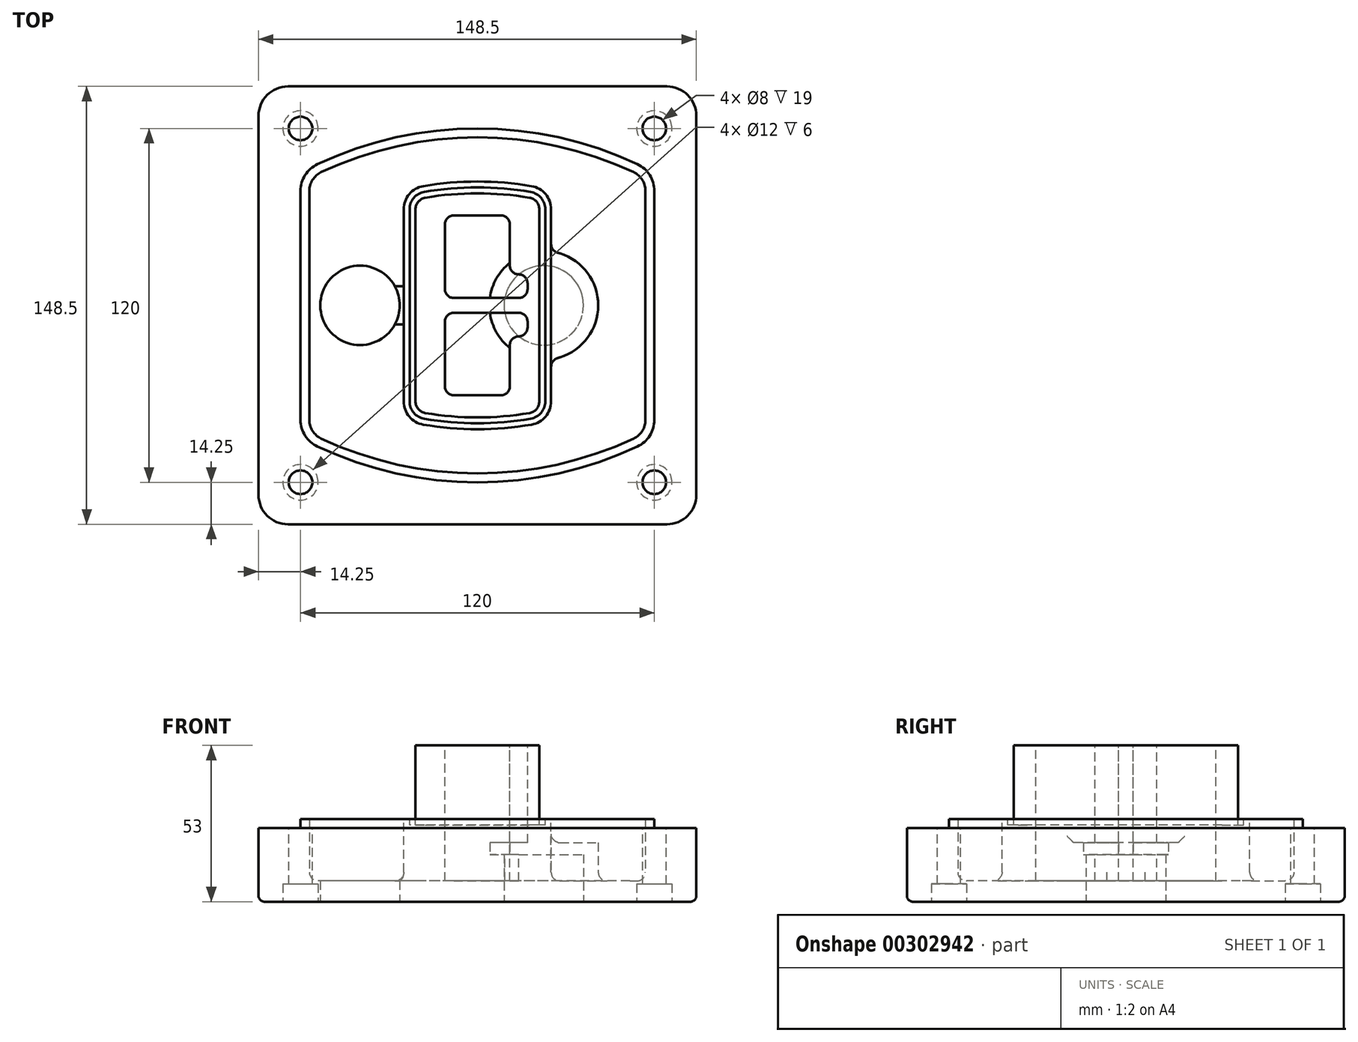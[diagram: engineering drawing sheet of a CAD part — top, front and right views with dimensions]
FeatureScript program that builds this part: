
annotation { "Feature Type Name" : "Feature", "Feature Type Description" : "" }
export const myFeature = defineFeature(function(context is Context, id is Id, definition is map)
    precondition{}
    {
        {
            var Q0;
            Q0=qCreatedBy(makeId("Top.planeOp"),FACE);
            var sketch = newSketch(context, id + "F0", { "sketchPlane" : qUnion([Q0])});
            skPoint(sketch, "E0.rect.middle", {"position": v(0, 0) * mm});
            skLineSegment(sketch, "E1.bottom", {"start": v(-64.25, -74.25) * mm, "end": v(64.25, -74.25) * mm});
            skLineSegment(sketch, "E1.top", {"start": v(-64.25, 74.25) * mm, "end": v(64.25, 74.25) * mm});
            skLineSegment(sketch, "E1.left", {"start": v(-74.25, -64.25) * mm, "end": v(-74.25, 64.25) * mm});
            skLineSegment(sketch, "E1.right", {"start": v(74.25, -64.25) * mm, "end": v(74.25, 64.25) * mm});
            skLineSegment(sketch, "E2", {"start": v(-74.25, 74.25) * mm, "end": v(74.25, -74.25) * mm, "construction": true});
            skLineSegment(sketch, "E3", {"start": v(74.25, 74.25) * mm, "end": v(-74.25, -74.25) * mm, "construction": true});
            skCircle(sketch, "E4", {"center": v(-60, 60) * mm, "radius": 4 * mm});
            skCircle(sketch, "E5", {"center": v(60, 60) * mm, "radius": 4 * mm});
            skCircle(sketch, "E6", {"center": v(60, -60) * mm, "radius": 4 * mm});
            skCircle(sketch, "E7", {"center": v(-60, -60) * mm, "radius": 4 * mm});
            skLineSegment(sketch, "E8", {"start": v(-60, 60) * mm, "end": v(60, 60) * mm, "construction": true});
            skLineSegment(sketch, "E9", {"start": v(60, 60) * mm, "end": v(60, -60) * mm, "construction": true});
            skLineSegment(sketch, "E10", {"start": v(60, -60) * mm, "end": v(-60, -60) * mm, "construction": true});
            skLineSegment(sketch, "E11", {"start": v(-60, -60) * mm, "end": v(-60, 60) * mm, "construction": true});
            skLineSegment(sketch, "E12", {"start": v(-60, 38.83) * mm, "end": v(-60, -38.83) * mm});
            skLineSegment(sketch, "E13", {"start": v(60, 38.83) * mm, "end": v(60, -38.83) * mm});
            skArc(sketch, "E14", {"start": v(54.26, 47.88) * mm, "mid": v(0, 60) * mm, "end": v(-54.26, 47.88) * mm});
            skArc(sketch, "E15", {"start": v(-54.26, -47.88) * mm, "mid": v(0, -60) * mm, "end": v(54.26, -47.88) * mm});
            skLineSegment(sketch, "E16", {"start": v(-60, 0) * mm, "end": v(60, 0) * mm, "construction": true});
            skPoint(sketch, "E17.visualSharp", {"position": v(-60, -45) * mm});
            skArc(sketch, "E17.filletArc", {"start": v(-60, -38.83) * mm, "mid": v(-58.44, -44.2) * mm, "end": v(-54.26, -47.88) * mm});
            skPoint(sketch, "E18.visualSharp", {"position": v(-60, 45) * mm});
            skArc(sketch, "E18.filletArc", {"start": v(-54.26, 47.88) * mm, "mid": v(-58.44, 44.2) * mm, "end": v(-60, 38.83) * mm});
            skPoint(sketch, "E19.visualSharp", {"position": v(60, 45) * mm});
            skArc(sketch, "E19.filletArc", {"start": v(60, 38.83) * mm, "mid": v(58.44, 44.2) * mm, "end": v(54.26, 47.88) * mm});
            skPoint(sketch, "E20.visualSharp", {"position": v(60, -45) * mm});
            skArc(sketch, "E20.filletArc", {"start": v(54.26, -47.88) * mm, "mid": v(58.44, -44.2) * mm, "end": v(60, -38.83) * mm});
            skPoint(sketch, "E21.visualSharp", {"position": v(-74.25, 74.25) * mm});
            skArc(sketch, "E21.filletArc", {"start": v(-64.25, 74.25) * mm, "mid": v(-71.32, 71.32) * mm, "end": v(-74.25, 64.25) * mm});
            skPoint(sketch, "E22.visualSharp", {"position": v(74.25, 74.25) * mm});
            skArc(sketch, "E22.filletArc", {"start": v(74.25, 64.25) * mm, "mid": v(71.32, 71.32) * mm, "end": v(64.25, 74.25) * mm});
            skPoint(sketch, "E23.visualSharp", {"position": v(74.25, -74.25) * mm});
            skArc(sketch, "E23.filletArc", {"start": v(64.25, -74.25) * mm, "mid": v(71.32, -71.32) * mm, "end": v(74.25, -64.25) * mm});
            skPoint(sketch, "E24.visualSharp", {"position": v(-74.25, -74.25) * mm});
            skArc(sketch, "E24.filletArc", {"start": v(-74.25, -64.25) * mm, "mid": v(-71.32, -71.32) * mm, "end": v(-64.25, -74.25) * mm});
            skArc(sketch, "E25.0", {"start": v(57, 38.83) * mm, "mid": v(55.9, 42.58) * mm, "end": v(52.98, 45.17) * mm});
            skLineSegment(sketch, "E25.1", {"start": v(57, 38.83) * mm, "end": v(57, -38.83) * mm});
            skArc(sketch, "E25.2", {"start": v(52.98, -45.17) * mm, "mid": v(55.9, -42.58) * mm, "end": v(57, -38.83) * mm});
            skArc(sketch, "E25.3", {"start": v(-52.98, -45.17) * mm, "mid": v(0, -57) * mm, "end": v(52.98, -45.17) * mm});
            skArc(sketch, "E25.4", {"start": v(-57, -38.83) * mm, "mid": v(-55.9, -42.58) * mm, "end": v(-52.98, -45.17) * mm});
            skArc(sketch, "E25.5", {"start": v(52.98, 45.17) * mm, "mid": v(0, 57) * mm, "end": v(-52.98, 45.17) * mm});
            skLineSegment(sketch, "E25.6", {"start": v(-57, 38.83) * mm, "end": v(-57, -38.83) * mm});
            skArc(sketch, "E25.7", {"start": v(-52.98, 45.17) * mm, "mid": v(-55.9, 42.58) * mm, "end": v(-57, 38.83) * mm});
            skArc(sketch, "E26.0", {"start": v(-55.96, 51.5) * mm, "mid": v(-61.82, 46.33) * mm, "end": v(-64, 38.83) * mm});
            skArc(sketch, "E26.1", {"start": v(55.96, 51.5) * mm, "mid": v(0, 64) * mm, "end": v(-55.96, 51.5) * mm});
            skArc(sketch, "E26.2", {"start": v(64, 38.83) * mm, "mid": v(61.82, 46.33) * mm, "end": v(55.96, 51.5) * mm});
            skLineSegment(sketch, "E26.3", {"start": v(64, 38.83) * mm, "end": v(64, -38.83) * mm});
            skArc(sketch, "E26.4", {"start": v(55.96, -51.5) * mm, "mid": v(61.82, -46.33) * mm, "end": v(64, -38.83) * mm});
            skLineSegment(sketch, "E26.5", {"start": v(-64, 38.83) * mm, "end": v(-64, -38.83) * mm});
            skArc(sketch, "E26.6", {"start": v(-55.96, -51.5) * mm, "mid": v(0, -64) * mm, "end": v(55.96, -51.5) * mm});
            skArc(sketch, "E26.7", {"start": v(-64, -38.83) * mm, "mid": v(-61.82, -46.33) * mm, "end": v(-55.96, -51.5) * mm});
            skSolve(sketch);
        }
        {
            var Q0;
            Q0=makeQuery(id+"F0.imprint","IMPRINT",FACE,{"disambiguationData":[TD([[makeQuery(id+"F0.imprint","IMPRINT",EDGE,{"derivedFrom":sQuery(id+"F0.wireOp",EDGE,"E1.bottom")}),1.0]])]});
            var Q1;
            Q1=makeQuery(id+"F0.imprint","IMPRINT",FACE,{"disambiguationData":[TD([[makeQuery(id+"F0.imprint","IMPRINT",EDGE,{"derivedFrom":sQuery(id+"F0.wireOp",EDGE,"E12")}),1.0]])]});
            var Q2;
            Q2=makeQuery(id+"F0.imprint","IMPRINT",FACE,{"disambiguationData":[TD([[makeQuery(id+"F0.imprint","IMPRINT",EDGE,{"derivedFrom":sQuery(id+"F0.wireOp",EDGE,"E25.0")}),1.0]])]});
            var Q3;
            Q3=makeQuery(id+"F0.imprint","IMPRINT",FACE,{"disambiguationData":[TD([[makeQuery(id+"F0.imprint","IMPRINT",EDGE,{"derivedFrom":sQuery(id+"F0.wireOp",EDGE,"E12")}),-1.0]])]});
            extrude(context, id + "F1", {"entities" : qUnion([Q0, Q1, Q2, Q3]), "oppositeDirection" : true, "depth" : 25 * mm});
        }
        {
            var Q0;
            Q0=makeQuery(id+"F0.imprint","IMPRINT",FACE,{"disambiguationData":[TD([[makeQuery(id+"F0.imprint","IMPRINT",EDGE,{"derivedFrom":sQuery(id+"F0.wireOp",EDGE,"E12")}),1.0]])]});
            extrude(context, id + "F2", {"entities" : qUnion([Q0]), "operationType" : NewBodyOperationType.ADD, "depth" : 3 * mm});
        }
        {
            var Q0;
            Q0=makeQuery(id+"F0.imprint","IMPRINT",FACE,{"disambiguationData":[TD([[makeQuery(id+"F0.imprint","IMPRINT",EDGE,{"derivedFrom":sQuery(id+"F0.wireOp",EDGE,"E25.0")}),1.0]])]});
            extrude(context, id + "F3", {"entities" : qUnion([Q0]), "operationType" : NewBodyOperationType.REMOVE, "oppositeDirection" : true, "depth" : 18 * mm});
        }
        {
            var Q0;
            Q0=makeQuery(id+"F2.opExtrude","CAP_FACE",FACE,{"disambiguationData":[OSD([sQuery(id+"F0.wireOp",EDGE,"E12"),sQuery(id+"F0.wireOp",EDGE,"E13"),sQuery(id+"F0.wireOp",EDGE,"E14"),sQuery(id+"F0.wireOp",EDGE,"E15"),sQuery(id+"F0.wireOp",EDGE,"E17.filletArc"),sQuery(id+"F0.wireOp",EDGE,"E18.filletArc"),sQuery(id+"F0.wireOp",EDGE,"E19.filletArc"),sQuery(id+"F0.wireOp",EDGE,"E20.filletArc"),sQuery(id+"F0.wireOp",EDGE,"E25.0"),sQuery(id+"F0.wireOp",EDGE,"E25.1"),sQuery(id+"F0.wireOp",EDGE,"E25.2"),sQuery(id+"F0.wireOp",EDGE,"E25.3"),sQuery(id+"F0.wireOp",EDGE,"E25.4"),sQuery(id+"F0.wireOp",EDGE,"E25.5"),sQuery(id+"F0.wireOp",EDGE,"E25.6"),sQuery(id+"F0.wireOp",EDGE,"E25.7")])],"isStart":false});
            var sketch = newSketch(context, id + "F4", { "sketchPlane" : qUnion([Q0])});
            skArc(sketch, "E27.0", {"start": v(-18.34, -40.45) * mm, "mid": v(0, -42) * mm, "end": v(18.34, -40.45) * mm});
            skArc(sketch, "E28.0", {"start": v(18.34, 40.45) * mm, "mid": v(0, 42) * mm, "end": v(-18.34, 40.45) * mm});
            skLineSegment(sketch, "E29", {"start": v(-25, 32.57) * mm, "end": v(-25, -32.57) * mm});
            skLineSegment(sketch, "E30", {"start": v(25, 32.57) * mm, "end": v(25, -32.57) * mm});
            skLineSegment(sketch, "E31", {"start": v(-25, 39.1) * mm, "end": v(25, 39.1) * mm, "construction": true});
            skLineSegment(sketch, "E32", {"start": v(-25, -39.1) * mm, "end": v(25, -39.1) * mm, "construction": true});
            skPoint(sketch, "E33.visualSharp", {"position": v(-25, 39.1) * mm});
            skArc(sketch, "E33.filletArc", {"start": v(-18.34, 40.45) * mm, "mid": v(-23.11, 37.73) * mm, "end": v(-25, 32.57) * mm});
            skPoint(sketch, "E34.visualSharp", {"position": v(25, 39.1) * mm});
            skArc(sketch, "E34.filletArc", {"start": v(25, 32.57) * mm, "mid": v(23.11, 37.73) * mm, "end": v(18.34, 40.45) * mm});
            skPoint(sketch, "E35.visualSharp", {"position": v(25, -39.1) * mm});
            skArc(sketch, "E35.filletArc", {"start": v(18.34, -40.45) * mm, "mid": v(23.11, -37.73) * mm, "end": v(25, -32.57) * mm});
            skPoint(sketch, "E36.visualSharp", {"position": v(-25, -39.1) * mm});
            skArc(sketch, "E36.filletArc", {"start": v(-25, -32.57) * mm, "mid": v(-23.11, -37.73) * mm, "end": v(-18.34, -40.45) * mm});
            skArc(sketch, "E37.0", {"start": v(52.98, 45.17) * mm, "mid": v(0, 57) * mm, "end": v(-52.98, 45.17) * mm});
            skArc(sketch, "E37.1", {"start": v(-52.98, 45.17) * mm, "mid": v(-55.9, 42.58) * mm, "end": v(-57, 38.83) * mm});
            skLineSegment(sketch, "E37.2", {"start": v(-57, 38.83) * mm, "end": v(-57, -38.83) * mm});
            skArc(sketch, "E37.3", {"start": v(-57, -38.83) * mm, "mid": v(-55.9, -42.58) * mm, "end": v(-52.98, -45.17) * mm});
            skArc(sketch, "E37.4", {"start": v(-52.98, -45.17) * mm, "mid": v(0, -57) * mm, "end": v(52.98, -45.17) * mm});
            skArc(sketch, "E37.5", {"start": v(52.98, -45.17) * mm, "mid": v(55.9, -42.58) * mm, "end": v(57, -38.83) * mm});
            skLineSegment(sketch, "E37.6", {"start": v(57, 38.83) * mm, "end": v(57, -38.83) * mm});
            skArc(sketch, "E37.7", {"start": v(57, 38.83) * mm, "mid": v(55.9, 42.58) * mm, "end": v(52.98, 45.17) * mm});
            skLineSegment(sketch, "E38.0", {"start": v(23, 32.57) * mm, "end": v(23, -32.57) * mm});
            skArc(sketch, "E38.1", {"start": v(18, -38.48) * mm, "mid": v(21.58, -36.44) * mm, "end": v(23, -32.57) * mm});
            skArc(sketch, "E38.2", {"start": v(-18, -38.48) * mm, "mid": v(0, -40) * mm, "end": v(18, -38.48) * mm});
            skArc(sketch, "E38.3", {"start": v(-23, -32.57) * mm, "mid": v(-21.58, -36.44) * mm, "end": v(-18, -38.48) * mm});
            skLineSegment(sketch, "E38.4", {"start": v(-23, 32.57) * mm, "end": v(-23, -32.57) * mm});
            skArc(sketch, "E38.5", {"start": v(23, 32.57) * mm, "mid": v(21.58, 36.44) * mm, "end": v(18, 38.48) * mm});
            skArc(sketch, "E38.6", {"start": v(-18, 38.48) * mm, "mid": v(-21.58, 36.44) * mm, "end": v(-23, 32.57) * mm});
            skArc(sketch, "E38.7", {"start": v(18, 38.48) * mm, "mid": v(0, 40) * mm, "end": v(-18, 38.48) * mm});
            skArc(sketch, "E39.0", {"start": v(21, 32.57) * mm, "mid": v(20.06, 35.15) * mm, "end": v(17.67, 36.5) * mm});
            skLineSegment(sketch, "E39.1", {"start": v(21, 32.57) * mm, "end": v(21, -32.57) * mm});
            skArc(sketch, "E39.2", {"start": v(17.67, -36.5) * mm, "mid": v(20.06, -35.15) * mm, "end": v(21, -32.57) * mm});
            skArc(sketch, "E39.3", {"start": v(-17.67, -36.5) * mm, "mid": v(0, -38) * mm, "end": v(17.67, -36.5) * mm});
            skArc(sketch, "E39.4", {"start": v(-21, -32.57) * mm, "mid": v(-20.06, -35.15) * mm, "end": v(-17.67, -36.5) * mm});
            skArc(sketch, "E39.5", {"start": v(17.67, 36.5) * mm, "mid": v(0, 38) * mm, "end": v(-17.67, 36.5) * mm});
            skLineSegment(sketch, "E39.6", {"start": v(-21, 32.57) * mm, "end": v(-21, -32.57) * mm});
            skArc(sketch, "E39.7", {"start": v(-17.67, 36.5) * mm, "mid": v(-20.06, 35.15) * mm, "end": v(-21, 32.57) * mm});
            skLineSegment(sketch, "E40", {"start": v(-25, 0) * mm, "end": v(25, 0) * mm, "construction": true});
            skLineSegment(sketch, "E41", {"start": v(-11, 5.5) * mm, "end": v(-11, 27.5) * mm});
            skLineSegment(sketch, "E42", {"start": v(-8, 30.5) * mm, "end": v(8, 30.5) * mm});
            skLineSegment(sketch, "E43", {"start": v(11, 27.5) * mm, "end": v(11, 13.5) * mm});
            skLineSegment(sketch, "E44", {"start": v(14, 10.5) * mm, "end": v(14, 10.5) * mm});
            skLineSegment(sketch, "E45", {"start": v(17, 7.5) * mm, "end": v(17, 5.5) * mm});
            skLineSegment(sketch, "E46", {"start": v(14, 2.5) * mm, "end": v(-8, 2.5) * mm});
            skPoint(sketch, "E47.visualSharp", {"position": v(-11, 30.5) * mm});
            skArc(sketch, "E47.filletArc", {"start": v(-8, 30.5) * mm, "mid": v(-10.12, 29.62) * mm, "end": v(-11, 27.5) * mm});
            skPoint(sketch, "E48.visualSharp", {"position": v(11, 30.5) * mm});
            skArc(sketch, "E48.filletArc", {"start": v(11, 27.5) * mm, "mid": v(10.12, 29.62) * mm, "end": v(8, 30.5) * mm});
            skPoint(sketch, "E49.visualSharp", {"position": v(11, 10.5) * mm});
            skArc(sketch, "E49.filletArc", {"start": v(11, 13.5) * mm, "mid": v(11.88, 11.38) * mm, "end": v(14, 10.5) * mm});
            skPoint(sketch, "E50.visualSharp", {"position": v(17, 10.5) * mm});
            skArc(sketch, "E50.filletArc", {"start": v(17, 7.5) * mm, "mid": v(16.12, 9.62) * mm, "end": v(14, 10.5) * mm});
            skPoint(sketch, "E51.visualSharp", {"position": v(17, 2.5) * mm});
            skArc(sketch, "E51.filletArc", {"start": v(14, 2.5) * mm, "mid": v(16.12, 3.38) * mm, "end": v(17, 5.5) * mm});
            skPoint(sketch, "E52.visualSharp", {"position": v(-11, 2.5) * mm});
            skArc(sketch, "E52.filletArc", {"start": v(-11, 5.5) * mm, "mid": v(-10.12, 3.38) * mm, "end": v(-8, 2.5) * mm});
            skLineSegment(sketch, "E53.0.MirrorCS", {"start": v(14, -2.5) * mm, "end": v(-8, -2.5) * mm});
            skArc(sketch, "E54.0.MirrorCS", {"start": v(-11, -5.5) * mm, "mid": v(-10.12, -3.38) * mm, "end": v(-8, -2.5) * mm});
            skLineSegment(sketch, "E55.0.MirrorCS", {"start": v(-11, -5.5) * mm, "end": v(-11, -27.5) * mm});
            skArc(sketch, "E56.0.MirrorCS", {"start": v(-8, -30.5) * mm, "mid": v(-10.12, -29.62) * mm, "end": v(-11, -27.5) * mm});
            skLineSegment(sketch, "E57.0.MirrorCS", {"start": v(-8, -30.5) * mm, "end": v(8, -30.5) * mm});
            skArc(sketch, "E58.0.MirrorCS", {"start": v(11, -27.5) * mm, "mid": v(10.12, -29.62) * mm, "end": v(8, -30.5) * mm});
            skLineSegment(sketch, "E59.0.MirrorCS", {"start": v(11, -27.5) * mm, "end": v(11, -13.5) * mm});
            skArc(sketch, "E60.0.MirrorCS", {"start": v(11, -13.5) * mm, "mid": v(11.88, -11.38) * mm, "end": v(14, -10.5) * mm});
            skArc(sketch, "E61.0.MirrorCS", {"start": v(17, -7.5) * mm, "mid": v(16.12, -9.62) * mm, "end": v(14, -10.5) * mm});
            skLineSegment(sketch, "E62.0.MirrorCS", {"start": v(17, -7.5) * mm, "end": v(17, -5.5) * mm});
            skArc(sketch, "E63.0.MirrorCS", {"start": v(14, -2.5) * mm, "mid": v(16.12, -3.38) * mm, "end": v(17, -5.5) * mm});
            skSolve(sketch);
        }
        {
            var Q0;
            Q0=makeQuery(id+"F4.imprint","IMPRINT",FACE,{"disambiguationData":[TD([[makeQuery(id+"F4.imprint","IMPRINT",EDGE,{"derivedFrom":sQuery(id+"F4.wireOp",EDGE,"E27.0")}),1.0]])]});
            var Q1;
            Q1=makeQuery(id+"F4.imprint","IMPRINT",FACE,{"disambiguationData":[TD([[makeQuery(id+"F4.imprint","IMPRINT",EDGE,{"derivedFrom":sQuery(id+"F4.wireOp",EDGE,"E38.0")}),-1.0]])]});
            var Q2;
            Q2=makeQuery(id+"F4.imprint","IMPRINT",FACE,{"disambiguationData":[TD([[makeQuery(id+"F4.imprint","IMPRINT",EDGE,{"derivedFrom":sQuery(id+"F4.wireOp",EDGE,"E39.0")}),1.0]])]});
            extrude(context, id + "F5", {"entities" : qUnion([Q0, Q1, Q2]), "operationType" : NewBodyOperationType.ADD, "endBound" : BoundingType.UP_TO_NEXT, "oppositeDirection" : true, "depth" : 25 * mm});
        }
        {
            var Q0;
            Q0=makeQuery(id+"F4.imprint","IMPRINT",FACE,{"disambiguationData":[TD([[makeQuery(id+"F4.imprint","IMPRINT",EDGE,{"derivedFrom":sQuery(id+"F4.wireOp",EDGE,"E38.0")}),-1.0]])]});
            extrude(context, id + "F6", {"entities" : qUnion([Q0]), "operationType" : NewBodyOperationType.REMOVE, "oppositeDirection" : true, "depth" : 2 * mm});
        }
        {
            var Q0;
            Q0=makeQuery(id+"F1.opExtrude","CAP_FACE",FACE,{"disambiguationData":[OSD([sQuery(id+"F0.wireOp",EDGE,"E1.bottom"),sQuery(id+"F0.wireOp",EDGE,"E1.top"),sQuery(id+"F0.wireOp",EDGE,"E1.left"),sQuery(id+"F0.wireOp",EDGE,"E1.right"),sQuery(id+"F0.wireOp",EDGE,"E4"),sQuery(id+"F0.wireOp",EDGE,"E5"),sQuery(id+"F0.wireOp",EDGE,"E6"),sQuery(id+"F0.wireOp",EDGE,"E7"),sQuery(id+"F0.wireOp",EDGE,"E21.filletArc"),sQuery(id+"F0.wireOp",EDGE,"E22.filletArc"),sQuery(id+"F0.wireOp",EDGE,"E23.filletArc"),sQuery(id+"F0.wireOp",EDGE,"E24.filletArc")])],"isStart":false});
            var sketch = newSketch(context, id + "F7", { "sketchPlane" : qUnion([Q0])});
            skCircle(sketch, "E64", {"center": v(22.5, 0) * mm, "radius": 13.47 * mm});
            skCircle(sketch, "E65", {"center": v(-39.81, 0) * mm, "radius": 13.47 * mm});
            skLineSegment(sketch, "E66", {"start": v(74.25, 0) * mm, "end": v(-74.25, 0) * mm});
            skCircle(sketch, "E67", {"center": v(22.5, 0) * mm, "radius": 18.47 * mm});
            skCircle(sketch, "E68", {"center": v(60, -60) * mm, "radius": 6 * mm});
            skCircle(sketch, "E69", {"center": v(-60, -60) * mm, "radius": 6 * mm});
            skCircle(sketch, "E70", {"center": v(-60, 60) * mm, "radius": 6 * mm});
            skCircle(sketch, "E71", {"center": v(60, 60) * mm, "radius": 6 * mm});
            skSolve(sketch);
        }
        {
            var Q0;
            {var subQ1=sQuery(id+"F7.wireOp",EDGE,"E66");var subQ4=sQuery(id+"F7.wireOp",EDGE,"E64");var subQ6=makeQuery(id+"F7.imprint","INTERSECT",VERTEX,{"disambiguationData":[OD(0.0)],"derivedFrom":[subQ4,subQ1]});Q0=makeQuery(id+"F7.imprint","IMPRINT",FACE,{"disambiguationData":[TD([[makeQuery(id+"F7.imprint","IMPRINT",EDGE,{"disambiguationData":[TD([[subQ6,-1.0]])],"derivedFrom":subQ4}),-1.0]])]});}
            var Q1;
            {var subQ0=sQuery(id+"F7.wireOp",EDGE,"E66");var subQ1=sQuery(id+"F7.wireOp",EDGE,"E64");var subQ3=makeQuery(id+"F7.imprint","INTERSECT",VERTEX,{"disambiguationData":[OD(0.0)],"derivedFrom":[subQ1,subQ0]});Q1=makeQuery(id+"F7.imprint","IMPRINT",FACE,{"disambiguationData":[TD([[makeQuery(id+"F7.imprint","IMPRINT",EDGE,{"disambiguationData":[TD([[subQ3,-1.0]])],"derivedFrom":subQ1}),1.0]])]});}
            var Q2;
            {var subQ0=sQuery(id+"F7.wireOp",EDGE,"E66");var subQ1=sQuery(id+"F7.wireOp",EDGE,"E64");var subQ3=makeQuery(id+"F7.imprint","INTERSECT",VERTEX,{"disambiguationData":[OD(0.0)],"derivedFrom":[subQ1,subQ0]});Q2=makeQuery(id+"F7.imprint","IMPRINT",FACE,{"disambiguationData":[TD([[makeQuery(id+"F7.imprint","IMPRINT",EDGE,{"disambiguationData":[TD([[subQ3,1.0]])],"derivedFrom":subQ1}),1.0]])]});}
            var Q3;
            {var subQ1=sQuery(id+"F7.wireOp",EDGE,"E66");var subQ4=sQuery(id+"F7.wireOp",EDGE,"E64");var subQ6=makeQuery(id+"F7.imprint","INTERSECT",VERTEX,{"disambiguationData":[OD(0.0)],"derivedFrom":[subQ4,subQ1]});Q3=makeQuery(id+"F7.imprint","IMPRINT",FACE,{"disambiguationData":[TD([[makeQuery(id+"F7.imprint","IMPRINT",EDGE,{"disambiguationData":[TD([[subQ6,1.0]])],"derivedFrom":subQ4}),-1.0]])]});}
            extrude(context, id + "F8", {"entities" : qUnion([Q0, Q1, Q2, Q3]), "operationType" : NewBodyOperationType.ADD, "oppositeDirection" : true, "depth" : 20 * mm});
        }
        {
            var Q0;
            {var subQ0=sQuery(id+"F7.wireOp",EDGE,"E66");var subQ1=sQuery(id+"F7.wireOp",EDGE,"E64");var subQ3=makeQuery(id+"F7.imprint","INTERSECT",VERTEX,{"disambiguationData":[OD(0.0)],"derivedFrom":[subQ1,subQ0]});Q0=makeQuery(id+"F7.imprint","IMPRINT",FACE,{"disambiguationData":[TD([[makeQuery(id+"F7.imprint","IMPRINT",EDGE,{"disambiguationData":[TD([[subQ3,-1.0]])],"derivedFrom":subQ1}),1.0]])]});}
            var Q1;
            {var subQ0=sQuery(id+"F7.wireOp",EDGE,"E66");var subQ1=sQuery(id+"F7.wireOp",EDGE,"E64");var subQ3=makeQuery(id+"F7.imprint","INTERSECT",VERTEX,{"disambiguationData":[OD(0.0)],"derivedFrom":[subQ1,subQ0]});Q1=makeQuery(id+"F7.imprint","IMPRINT",FACE,{"disambiguationData":[TD([[makeQuery(id+"F7.imprint","IMPRINT",EDGE,{"disambiguationData":[TD([[subQ3,1.0]])],"derivedFrom":subQ1}),1.0]])]});}
            extrude(context, id + "F9", {"entities" : qUnion([Q0, Q1]), "operationType" : NewBodyOperationType.REMOVE, "oppositeDirection" : true, "depth" : 16 * mm});
        }
        {
            var Q0;
            {var subQ0=sQuery(id+"F7.wireOp",EDGE,"E66");var subQ1=sQuery(id+"F7.wireOp",EDGE,"E65");var subQ3=makeQuery(id+"F7.imprint","INTERSECT",VERTEX,{"disambiguationData":[OD(0.0)],"derivedFrom":[subQ1,subQ0]});Q0=makeQuery(id+"F7.imprint","IMPRINT",FACE,{"disambiguationData":[TD([[makeQuery(id+"F7.imprint","IMPRINT",EDGE,{"disambiguationData":[TD([[subQ3,-1.0]])],"derivedFrom":subQ1}),1.0]])]});}
            var Q1;
            {var subQ0=sQuery(id+"F7.wireOp",EDGE,"E66");var subQ1=sQuery(id+"F7.wireOp",EDGE,"E65");var subQ3=makeQuery(id+"F7.imprint","INTERSECT",VERTEX,{"disambiguationData":[OD(0.0)],"derivedFrom":[subQ1,subQ0]});Q1=makeQuery(id+"F7.imprint","IMPRINT",FACE,{"disambiguationData":[TD([[makeQuery(id+"F7.imprint","IMPRINT",EDGE,{"disambiguationData":[TD([[subQ3,1.0]])],"derivedFrom":subQ1}),1.0]])]});}
            extrude(context, id + "F10", {"entities" : qUnion([Q0, Q1]), "operationType" : NewBodyOperationType.REMOVE, "oppositeDirection" : true, "depth" : 25 * mm});
        }
        {
            var Q0;
            Q0=makeQuery(id+"F7.imprint","IMPRINT",FACE,{"disambiguationData":[TD([[makeQuery(id+"F7.imprint","IMPRINT",EDGE,{"derivedFrom":sQuery(id+"F7.wireOp",EDGE,"E68")}),1.0]])]});
            var Q1;
            Q1=makeQuery(id+"F7.imprint","IMPRINT",FACE,{"disambiguationData":[TD([[makeQuery(id+"F7.imprint","IMPRINT",EDGE,{"derivedFrom":makeQuery(id+"F1.opExtrude","CAP_EDGE",EDGE,{"disambiguationData":[OSD([sQuery(id+"F0.wireOp",EDGE,"E5")])],"isStart":false})}),-1.0]])]});
            var Q2;
            Q2=makeQuery(id+"F7.imprint","IMPRINT",FACE,{"disambiguationData":[TD([[makeQuery(id+"F7.imprint","IMPRINT",EDGE,{"derivedFrom":sQuery(id+"F7.wireOp",EDGE,"E69")}),1.0]])]});
            var Q3;
            Q3=makeQuery(id+"F7.imprint","IMPRINT",FACE,{"disambiguationData":[TD([[makeQuery(id+"F7.imprint","IMPRINT",EDGE,{"derivedFrom":makeQuery(id+"F1.opExtrude","CAP_EDGE",EDGE,{"disambiguationData":[OSD([sQuery(id+"F0.wireOp",EDGE,"E4")])],"isStart":false})}),-1.0]])]});
            var Q4;
            Q4=makeQuery(id+"F7.imprint","IMPRINT",FACE,{"disambiguationData":[TD([[makeQuery(id+"F7.imprint","IMPRINT",EDGE,{"derivedFrom":sQuery(id+"F7.wireOp",EDGE,"E70")}),1.0]])]});
            var Q5;
            Q5=makeQuery(id+"F7.imprint","IMPRINT",FACE,{"disambiguationData":[TD([[makeQuery(id+"F7.imprint","IMPRINT",EDGE,{"derivedFrom":makeQuery(id+"F1.opExtrude","CAP_EDGE",EDGE,{"disambiguationData":[OSD([sQuery(id+"F0.wireOp",EDGE,"E7")])],"isStart":false})}),-1.0]])]});
            var Q6;
            Q6=makeQuery(id+"F7.imprint","IMPRINT",FACE,{"disambiguationData":[TD([[makeQuery(id+"F7.imprint","IMPRINT",EDGE,{"derivedFrom":sQuery(id+"F7.wireOp",EDGE,"E71")}),1.0]])]});
            var Q7;
            Q7=makeQuery(id+"F7.imprint","IMPRINT",FACE,{"disambiguationData":[TD([[makeQuery(id+"F7.imprint","IMPRINT",EDGE,{"derivedFrom":makeQuery(id+"F1.opExtrude","CAP_EDGE",EDGE,{"disambiguationData":[OSD([sQuery(id+"F0.wireOp",EDGE,"E6")])],"isStart":false})}),-1.0]])]});
            extrude(context, id + "F11", {"entities" : qUnion([Q0, Q1, Q2, Q3, Q4, Q5, Q6, Q7]), "operationType" : NewBodyOperationType.REMOVE, "oppositeDirection" : true, "depth" : 6 * mm});
        }
        {
            var Q0;
            Q0=makeQuery(id+"F9.boolean.opBoolean","COPY",FACE,{"derivedFrom":makeQuery(id+"F9.opExtrude","CAP_FACE",FACE,{"disambiguationData":[OSD([sQuery(id+"F7.wireOp",EDGE,"E64")])],"isStart":false})});
            var sketch = newSketch(context, id + "F12", { "sketchPlane" : qUnion([Q0])});
            skArc(sketch, "E72.0", {"start": v(11, 14.45) * mm, "mid": v(6.45, 9.13) * mm, "end": v(4.2, 2.5) * mm});
            skArc(sketch, "E72.1", {"start": v(4.2, -2.5) * mm, "mid": v(6.45, -9.13) * mm, "end": v(11, -14.45) * mm});
            skLineSegment(sketch, "E73", {"start": v(4.2, -2.5) * mm, "end": v(14, -2.5) * mm});
            skLineSegment(sketch, "E74.0", {"start": v(14, 2.5) * mm, "end": v(4.2, 2.5) * mm});
            skArc(sketch, "E74.1", {"start": v(14, 2.5) * mm, "mid": v(16.12, 3.38) * mm, "end": v(17, 5.5) * mm});
            skLineSegment(sketch, "E74.2", {"start": v(17, 7.5) * mm, "end": v(17, 5.5) * mm});
            skArc(sketch, "E74.3", {"start": v(17, 7.5) * mm, "mid": v(16.12, 9.62) * mm, "end": v(14, 10.5) * mm});
            skArc(sketch, "E74.4", {"start": v(11, 13.5) * mm, "mid": v(11.88, 11.38) * mm, "end": v(14, 10.5) * mm});
            skLineSegment(sketch, "E74.5", {"start": v(11, 14.45) * mm, "end": v(11, 13.5) * mm});
            skLineSegment(sketch, "E74.7", {"start": v(14, -2.5) * mm, "end": v(4.2, -2.5) * mm});
            skArc(sketch, "E74.8", {"start": v(14, -2.5) * mm, "mid": v(16.12, -3.38) * mm, "end": v(17, -5.5) * mm});
            skLineSegment(sketch, "E74.9", {"start": v(17, -7.5) * mm, "end": v(17, -5.5) * mm});
            skArc(sketch, "E74.10", {"start": v(17, -7.5) * mm, "mid": v(16.12, -9.62) * mm, "end": v(14, -10.5) * mm});
            skArc(sketch, "E74.11", {"start": v(11, -13.5) * mm, "mid": v(11.88, -11.38) * mm, "end": v(14, -10.5) * mm});
            skLineSegment(sketch, "E74.12", {"start": v(11, -14.45) * mm, "end": v(11, -13.5) * mm});
            skPoint(sketch, "E75.orphan", {"position": v(11, -27.5) * mm});
            skPoint(sketch, "E76.orphan", {"position": v(-8, -2.5) * mm});
            skPoint(sketch, "E77.orphan", {"position": v(-8, 2.5) * mm});
            skPoint(sketch, "E78.orphan", {"position": v(11, 27.5) * mm});
            skSolve(sketch);
        }
        {
            var Q0;
            {var subQ7=sQuery(id+"F12.wireOp",EDGE,"E72.0");var subQ14=sQuery(id+"F12.wireOp",EDGE,"E72.1");var subQ16=sQuery(id+"F12.wireOp",EDGE,"E74.1");var subQ18=sQuery(id+"F12.wireOp",EDGE,"E74.8");Q0=qUnion([makeQuery(id+"F12.imprint","IMPRINT",FACE,{"disambiguationData":[TD([[makeQuery(id+"F12.imprint","IMPRINT",EDGE,{"derivedFrom":subQ7}),1.0]])]}),makeQuery(id+"F12.imprint","IMPRINT",FACE,{"disambiguationData":[TD([[makeQuery(id+"F12.imprint","IMPRINT",EDGE,{"derivedFrom":subQ14}),1.0]])]}),makeQuery(id+"F12.imprint","IMPRINT",FACE,{"disambiguationData":[TD([[makeQuery(id+"F12.imprint","IMPRINT",EDGE,{"derivedFrom":subQ16}),1.0]])]}),makeQuery(id+"F12.imprint","IMPRINT",FACE,{"disambiguationData":[TD([[makeQuery(id+"F12.imprint","IMPRINT",EDGE,{"derivedFrom":subQ18}),-1.0]])]})]);}
            var Q1;
            Q1=makeQuery(id+"F5.boolean.opBoolean","SPLIT",FACE,{"disambiguationData":[TD([makeQuery(id+"F5.opExtrude","SWEPT_FACE",FACE,{"disambiguationData":[OSD([sQuery(id+"F4.wireOp",EDGE,"E41")])]})])],"derivedFrom":makeQuery(id+"F3.boolean.opBoolean","COPY",FACE,{"derivedFrom":makeQuery(id+"F3.opExtrude","CAP_FACE",FACE,{"disambiguationData":[OSD([sQuery(id+"F0.wireOp",EDGE,"E25.0"),sQuery(id+"F0.wireOp",EDGE,"E25.1"),sQuery(id+"F0.wireOp",EDGE,"E25.2"),sQuery(id+"F0.wireOp",EDGE,"E25.3"),sQuery(id+"F0.wireOp",EDGE,"E25.4"),sQuery(id+"F0.wireOp",EDGE,"E25.5"),sQuery(id+"F0.wireOp",EDGE,"E25.6"),sQuery(id+"F0.wireOp",EDGE,"E25.7")])],"isStart":false})})});
            extrude(context, id + "F13", {"entities" : qUnion([Q0]), "operationType" : NewBodyOperationType.REMOVE, "endBound" : BoundingType.UP_TO_SURFACE, "endBoundEntityFace" : qUnion([Q1]), "depth" : 25 * mm});
        }
        {
            var Q0;
            Q0=makeQuery(id+"F3.boolean.opBoolean","COPY",EDGE,{"derivedFrom":makeQuery(id+"F3.opExtrude","CAP_EDGE",EDGE,{"disambiguationData":[OSD([sQuery(id+"F0.wireOp",EDGE,"E25.6")])],"isStart":false})});
            var Q1;
            Q1=makeQuery(id+"F8.boolean.opBoolean","INTERSECT",EDGE,{"derivedFrom":[makeQuery(id+"F5.opExtrude","SWEPT_FACE",FACE,{"disambiguationData":[OSD([sQuery(id+"F4.wireOp",EDGE,"E30")])]}),makeQuery(id+"F8.opExtrude","CAP_FACE",FACE,{"disambiguationData":[OSD([sQuery(id+"F7.wireOp",EDGE,"E67")])],"isStart":false})]});
            var Q2;
            Q2=makeQuery(id+"F8.boolean.opBoolean","INTERSECT",EDGE,{"disambiguationData":[OD(1.0)],"derivedFrom":[makeQuery(id+"F5.opExtrude","SWEPT_FACE",FACE,{"disambiguationData":[OSD([sQuery(id+"F4.wireOp",EDGE,"E30")])]}),makeQuery(id+"F8.opExtrude","SWEPT_FACE",FACE,{"disambiguationData":[OSD([sQuery(id+"F7.wireOp",EDGE,"E67")])]})]});
            var Q3;
            {var subQ0=sQuery(id+"F4.wireOp",EDGE,"E30");Q3=makeQuery(id+"F8.boolean.opBoolean","SPLIT",EDGE,{"disambiguationData":[TD([makeQuery(id+"F5.opExtrude","SWEPT_FACE",FACE,{"disambiguationData":[OSD([sQuery(id+"F4.wireOp",EDGE,"E35.filletArc")])]})])],"derivedFrom":makeQuery(id+"F5.opExtrude","CAP_EDGE",EDGE,{"disambiguationData":[OSD([subQ0])],"isStart":false})});}
            var Q4;
            {var subQ0=sQuery(id+"F0.wireOp",EDGE,"E25.7");var subQ1=sQuery(id+"F0.wireOp",EDGE,"E25.1");var subQ2=sQuery(id+"F0.wireOp",EDGE,"E25.6");var subQ3=sQuery(id+"F0.wireOp",EDGE,"E25.5");var subQ4=sQuery(id+"F0.wireOp",EDGE,"E25.4");var subQ5=sQuery(id+"F0.wireOp",EDGE,"E25.0");var subQ6=sQuery(id+"F0.wireOp",EDGE,"E25.2");var subQ7=sQuery(id+"F0.wireOp",EDGE,"E25.3");Q4=makeQuery(id+"F8.boolean.opBoolean","INTERSECT",EDGE,{"derivedFrom":[makeQuery(id+"F5.boolean.opBoolean","SPLIT",FACE,{"disambiguationData":[TD([makeQuery(id+"F2.opExtrude","SWEPT_FACE",FACE,{"disambiguationData":[OSD([subQ5])]})])],"derivedFrom":makeQuery(id+"F3.boolean.opBoolean","COPY",FACE,{"derivedFrom":makeQuery(id+"F3.opExtrude","CAP_FACE",FACE,{"disambiguationData":[OSD([subQ5,subQ1,subQ6,subQ7,subQ4,subQ3,subQ2,subQ0])],"isStart":false})})}),makeQuery(id+"F8.opExtrude","SWEPT_FACE",FACE,{"disambiguationData":[OSD([sQuery(id+"F7.wireOp",EDGE,"E67")])]})]});}
            var Q5;
            Q5=makeQuery(id+"F8.boolean.opBoolean","INTERSECT",EDGE,{"disambiguationData":[OD(0.0)],"derivedFrom":[makeQuery(id+"F5.opExtrude","SWEPT_FACE",FACE,{"disambiguationData":[OSD([sQuery(id+"F4.wireOp",EDGE,"E30")])]}),makeQuery(id+"F8.opExtrude","SWEPT_FACE",FACE,{"disambiguationData":[OSD([sQuery(id+"F7.wireOp",EDGE,"E67")])]})]});
            fillet(context, id + "F14", {"entities" : qUnion([Q0, Q1, Q2, Q3, Q4, Q5]), "radius" : 3 * mm, "tangentPropagation" : true, "allowEdgeOverflow" : false});
        }
        {
            var Q0;
            Q0=makeQuery(id+"F1.opExtrude","CAP_EDGE",EDGE,{"disambiguationData":[OSD([sQuery(id+"F0.wireOp",EDGE,"E1.bottom")])],"isStart":false});
            fillet(context, id + "F15", {"entities" : qUnion([Q0]), "radius" : 2 * mm, "tangentPropagation" : true, "allowEdgeOverflow" : false});
        }
        {
            var Q0;
            {var subQ0=sQuery(id+"F4.wireOp",EDGE,"E63.0.MirrorCS");var subQ1=sQuery(id+"F4.wireOp",EDGE,"E62.0.MirrorCS");var subQ2=sQuery(id+"F4.wireOp",EDGE,"E61.0.MirrorCS");var subQ3=sQuery(id+"F4.wireOp",EDGE,"E60.0.MirrorCS");var subQ4=sQuery(id+"F4.wireOp",EDGE,"E59.0.MirrorCS");var subQ5=sQuery(id+"F4.wireOp",EDGE,"E58.0.MirrorCS");var subQ6=sQuery(id+"F4.wireOp",EDGE,"E57.0.MirrorCS");var subQ7=sQuery(id+"F4.wireOp",EDGE,"E56.0.MirrorCS");var subQ8=sQuery(id+"F4.wireOp",EDGE,"E55.0.MirrorCS");var subQ9=sQuery(id+"F4.wireOp",EDGE,"E54.0.MirrorCS");var subQ10=sQuery(id+"F4.wireOp",EDGE,"E53.0.MirrorCS");var subQ11=sQuery(id+"F4.wireOp",EDGE,"E52.filletArc");var subQ12=sQuery(id+"F4.wireOp",EDGE,"E45");var subQ13=sQuery(id+"F4.wireOp",EDGE,"E43");var subQ14=sQuery(id+"F4.wireOp",EDGE,"E42");var subQ15=sQuery(id+"F4.wireOp",EDGE,"E41");var subQ16=sQuery(id+"F4.wireOp",EDGE,"E46");var subQ17=sQuery(id+"F4.wireOp",EDGE,"E47.filletArc");var subQ18=sQuery(id+"F4.wireOp",EDGE,"E48.filletArc");var subQ19=sQuery(id+"F4.wireOp",EDGE,"E49.filletArc");var subQ20=sQuery(id+"F4.wireOp",EDGE,"E50.filletArc");var subQ21=sQuery(id+"F4.wireOp",EDGE,"E51.filletArc");Q0=makeQuery(id+"F6.boolean.opBoolean","SPLIT",FACE,{"disambiguationData":[TD([makeQuery(id+"F5.opExtrude","SWEPT_FACE",FACE,{"disambiguationData":[OSD([subQ15])]})])],"derivedFrom":makeQuery(id+"F5.opExtrude","CAP_FACE",FACE,{"disambiguationData":[OSD([sQuery(id+"F4.wireOp",EDGE,"E27.0"),sQuery(id+"F4.wireOp",EDGE,"E28.0"),sQuery(id+"F4.wireOp",EDGE,"E29"),sQuery(id+"F4.wireOp",EDGE,"E30"),sQuery(id+"F4.wireOp",EDGE,"E33.filletArc"),sQuery(id+"F4.wireOp",EDGE,"E34.filletArc"),sQuery(id+"F4.wireOp",EDGE,"E35.filletArc"),sQuery(id+"F4.wireOp",EDGE,"E36.filletArc"),subQ15,subQ14,subQ13,subQ12,subQ16,subQ17,subQ18,subQ19,subQ20,subQ21,subQ11,subQ10,subQ9,subQ8,subQ7,subQ6,subQ5,subQ4,subQ3,subQ2,subQ1,subQ0])],"isStart":true})});}
            extrude(context, id + "F16", {"entities" : qUnion([Q0]), "operationType" : NewBodyOperationType.ADD, "depth" : 25 * mm});
        }
    });
